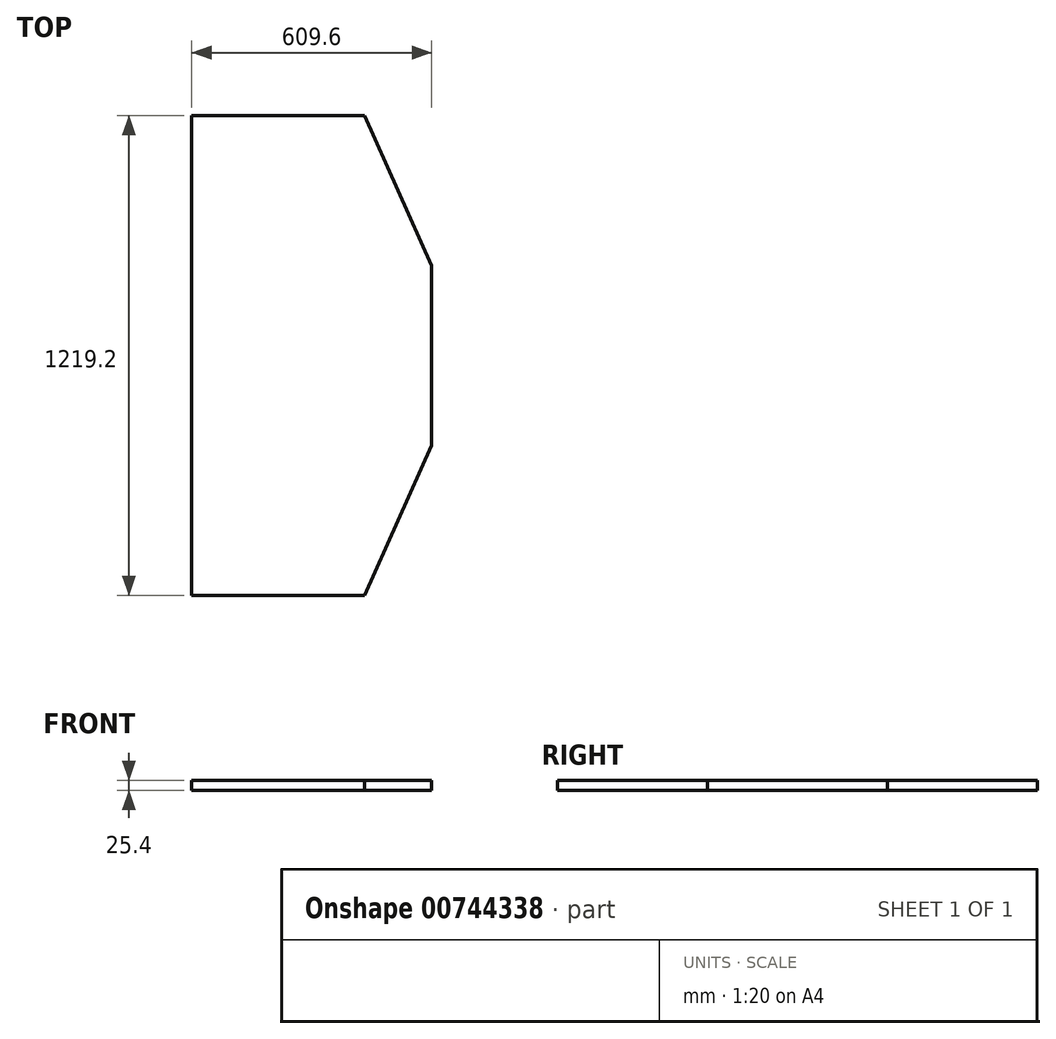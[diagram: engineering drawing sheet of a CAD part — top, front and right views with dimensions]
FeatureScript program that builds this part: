
annotation { "Feature Type Name" : "Feature", "Feature Type Description" : "" }
export const myFeature = defineFeature(function(context is Context, id is Id, definition is map)
    precondition{}
    {
        {
            var Q0;
            Q0=qCreatedBy(makeId("Top.planeOp"),FACE);
            var sketch = newSketch(context, id + "F0", { "sketchPlane" : qUnion([Q0])});
            skLineSegment(sketch, "E0.bottom", {"start": v(304.8, -609.6) * mm, "end": v(-304.8, -609.6) * mm});
            skLineSegment(sketch, "E0.top", {"start": v(304.8, 609.6) * mm, "end": v(-304.8, 609.6) * mm});
            skLineSegment(sketch, "E0.left", {"start": v(304.8, -609.6) * mm, "end": v(304.8, 609.6) * mm});
            skLineSegment(sketch, "E0.right", {"start": v(-304.8, -609.6) * mm, "end": v(-304.8, 609.6) * mm});
            skPoint(sketch, "E0.middle", {"position": v(0, 0) * mm});
            skLineSegment(sketch, "E1", {"start": v(0, 609.6) * mm, "end": v(0, -609.6) * mm});
            skLineSegment(sketch, "E2", {"start": v(133.8, 609.6) * mm, "end": v(304.8, 228.6) * mm});
            skLineSegment(sketch, "E3", {"start": v(304.8, 228.6) * mm, "end": v(304.8, -228.6) * mm});
            skLineSegment(sketch, "E4", {"start": v(304.8, -228.6) * mm, "end": v(133.8, -609.6) * mm});
            skPoint(sketch, "E5", {"position": v(304.8, 0) * mm});
            skSolve(sketch);
        }
        {
            var Q0;
            {var subQ0=sQuery(id+"F0.wireOp",EDGE,"E0.right");Q0=makeQuery(id+"F0.imprint","IMPRINT",FACE,{"disambiguationData":[TD([[makeQuery(id+"F0.imprint","IMPRINT",EDGE,{"derivedFrom":subQ0}),-1.0]])]});}
            var Q1;
            {var subQ1=sQuery(id+"F0.wireOp",EDGE,"E1");Q1=makeQuery(id+"F0.imprint","IMPRINT",FACE,{"disambiguationData":[TD([[makeQuery(id+"F0.imprint","IMPRINT",EDGE,{"derivedFrom":subQ1}),1.0]])]});}
            extrude(context, id + "F1", {"entities" : qUnion([Q0, Q1]), "depth" : 25.4 * mm, "offsetDistance" : 25.4 * mm});
        }
    });
